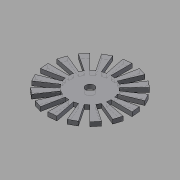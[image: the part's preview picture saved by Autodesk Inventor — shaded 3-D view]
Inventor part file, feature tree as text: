
AUTODESK INVENTOR PART (.ipt)
format: ipt  version: 2015 (Build 190159000, 159)  size: 172,544 bytes
history: native  units: in
note: dims shown in document units (in); Inventor stores cm internally (conversion verified against a paired STEP export)
features: other x3, sketch x1
ambient origin geometry x8: Origin, YZ Plane, XZ Plane, XY Plane, X Axis, Y Axis, Z Axis, Center Point
bodies: Solid1 (feature_tree)
feature tree (4):
  other  "encoder.ipt"
  other  "Solid2::encoder.ipt"
  other  "TaggingFeature1"
  sketch  "Sketch1"  dims[d0=0.3937in]
